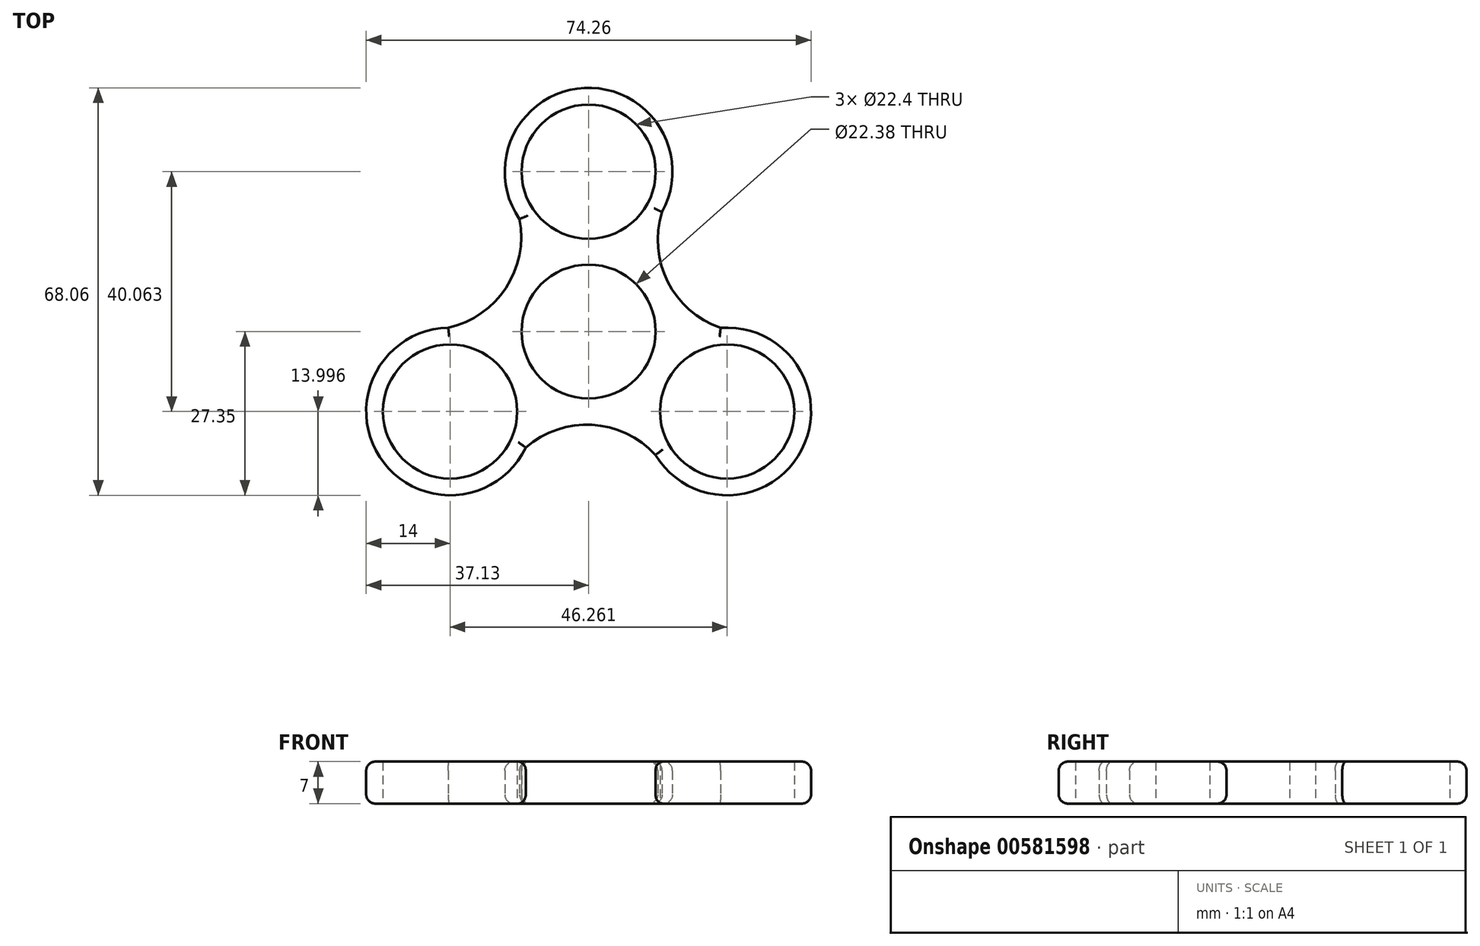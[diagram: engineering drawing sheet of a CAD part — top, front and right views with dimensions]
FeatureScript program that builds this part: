
annotation { "Feature Type Name" : "Feature", "Feature Type Description" : "" }
export const myFeature = defineFeature(function(context is Context, id is Id, definition is map)
    precondition{}
    {
        {
            var Q0;
            Q0=qCreatedBy(makeId("Top.planeOp"),FACE);
            var sketch = newSketch(context, id + "F0", { "sketchPlane" : qUnion([Q0])});
            skCircle(sketch, "E0", {"center": v(0, 0) * mm, "radius": 11.2 * mm});
            skCircle(sketch, "E1", {"center": v(0, 26.7) * mm, "radius": 11.2 * mm});
            skArc(sketch, "E2", {"start": v(12.28, 19.98) * mm, "mid": v(-0.7, 40.7) * mm, "end": v(-11.54, 18.79) * mm});
            skArc(sketch, "E3.1.0", {"start": v(-23.44, 0.64) * mm, "mid": v(-34.9, -20.95) * mm, "end": v(-10.5, -19.4) * mm});
            skCircle(sketch, "E3.1.1", {"center": v(-23.13, -13.35) * mm, "radius": 11.2 * mm});
            skArc(sketch, "E3.2.0", {"start": v(11.16, -20.62) * mm, "mid": v(35.59, -19.74) * mm, "end": v(22.04, 0.6) * mm});
            skCircle(sketch, "E3.2.1", {"center": v(23.13, -13.35) * mm, "radius": 11.2 * mm});
            skArc(sketch, "E4", {"start": v(12.28, 19.98) * mm, "mid": v(13.21, 8.3) * mm, "end": v(22.04, 0.6) * mm});
            skArc(sketch, "E5.1.0", {"start": v(-23.44, 0.64) * mm, "mid": v(-13.8, 7.3) * mm, "end": v(-11.54, 18.79) * mm});
            skArc(sketch, "E5.2.0", {"start": v(11.16, -20.62) * mm, "mid": v(0.58, -15.6) * mm, "end": v(-10.5, -19.4) * mm});
            skSolve(sketch);
        }
        {
            var Q0;
            Q0=makeQuery(id+"F0.imprint","IMPRINT",FACE,{"disambiguationData":[TD([[makeQuery(id+"F0.imprint","IMPRINT",EDGE,{"derivedFrom":sQuery(id+"F0.wireOp",EDGE,"E0")}),-1.0]])]});
            extrude(context, id + "F1", {"entities" : qUnion([Q0]), "depth" : 7 * mm, "offsetDistance" : 25 * mm});
        }
        {
            var Q0;
            Q0=makeQuery(id+"F1.opExtrude","CAP_EDGE",EDGE,{"disambiguationData":[OSD([sQuery(id+"F0.wireOp",EDGE,"E5.2.0")])],"isStart":false});
            var Q1;
            Q1=makeQuery(id+"F1.opExtrude","CAP_EDGE",EDGE,{"disambiguationData":[OSD([sQuery(id+"F0.wireOp",EDGE,"E5.2.0")])],"isStart":true});
            var Q2;
            Q2=makeQuery(id+"F1.opExtrude","CAP_EDGE",EDGE,{"disambiguationData":[OSD([sQuery(id+"F0.wireOp",EDGE,"E3.1.0")])],"isStart":false});
            var Q3;
            Q3=makeQuery(id+"F1.opExtrude","CAP_EDGE",EDGE,{"disambiguationData":[OSD([sQuery(id+"F0.wireOp",EDGE,"E5.1.0")])],"isStart":false});
            var Q4;
            Q4=makeQuery(id+"F1.opExtrude","CAP_EDGE",EDGE,{"disambiguationData":[OSD([sQuery(id+"F0.wireOp",EDGE,"E2")])],"isStart":false});
            var Q5;
            Q5=makeQuery(id+"F1.opExtrude","CAP_EDGE",EDGE,{"disambiguationData":[OSD([sQuery(id+"F0.wireOp",EDGE,"E4")])],"isStart":false});
            var Q6;
            Q6=makeQuery(id+"F1.opExtrude","CAP_EDGE",EDGE,{"disambiguationData":[OSD([sQuery(id+"F0.wireOp",EDGE,"E3.2.0")])],"isStart":false});
            fillet(context, id + "F2", {"entities" : qUnion([Q0, Q1, Q2, Q3, Q4, Q5, Q6]), "radius" : 1.5 * mm, "tangentPropagation" : true, "allowEdgeOverflow" : false});
        }
        {
            var Q0;
            Q0=makeQuery(id+"F1.opExtrude","CAP_EDGE",EDGE,{"disambiguationData":[OSD([sQuery(id+"F0.wireOp",EDGE,"E3.1.0")])],"isStart":true});
            var Q1;
            Q1=makeQuery(id+"F1.opExtrude","CAP_EDGE",EDGE,{"disambiguationData":[OSD([sQuery(id+"F0.wireOp",EDGE,"E5.1.0")])],"isStart":true});
            var Q2;
            Q2=makeQuery(id+"F1.opExtrude","CAP_EDGE",EDGE,{"disambiguationData":[OSD([sQuery(id+"F0.wireOp",EDGE,"E2")])],"isStart":true});
            var Q3;
            Q3=makeQuery(id+"F1.opExtrude","CAP_EDGE",EDGE,{"disambiguationData":[OSD([sQuery(id+"F0.wireOp",EDGE,"E4")])],"isStart":true});
            var Q4;
            Q4=makeQuery(id+"F1.opExtrude","CAP_EDGE",EDGE,{"disambiguationData":[OSD([sQuery(id+"F0.wireOp",EDGE,"E3.2.0")])],"isStart":true});
            fillet(context, id + "F3", {"entities" : qUnion([Q0, Q1, Q2, Q3, Q4]), "radius" : 1.5 * mm, "tangentPropagation" : true, "allowEdgeOverflow" : false});
        }
    });
